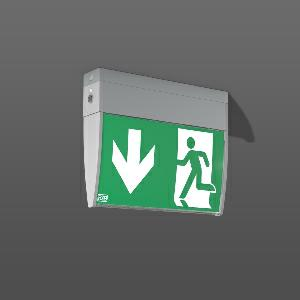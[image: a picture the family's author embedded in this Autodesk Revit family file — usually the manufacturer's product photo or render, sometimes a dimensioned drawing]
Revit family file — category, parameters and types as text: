
# Revit family: gsun_d_652219_004_79a5
name_source: partatom
category: Lighting Fixtures
units: mm (PartAtom-declared; Revit-internal decimal feet)

## family parameters
Cut with Voids When Loaded = No
Host = Face
Light Source = No
Part Type = Normal
Room Calculation Point = No
Round Connector Dimension = Use Diameter
Shared = No

## types (1)
- GSUN D
    Apparent Load = 0 VA
    Approval mark = CE
    Default Elevation = 1800 mm
    Description = Series: GSUN D
Luminaire for escape route identification. Housing: extruded aluminium profile, powder-coated. 4 legends and 1 white lay in plastic sheet included. Universal mounting kit for ceiling and wall surface mounting. Electronic ballast included. Self-contained system with automatic self-test. With NFC programming interface. 
Colour: silver
Length: 247 mm
Width: 45 mm
Height: 200 mm
Weight: 0.9 kg
Operating mode: maintained power mode
Viewing Distance: 24 m
Duration time: 1 h, 3 h, 8 h
Lamp: LED
Socket: without socket
Colour temperature: 4000K
System power: 2 W
Control gear: Regulated power supply
Protection class: I
Type of protection: IP 30
    Height = 200 mm
    Lamp = 0 x
    Length = 247 mm
    Luminous efficacy = 0 lm/W
    Manufacturer = RZB
    ModVariant = No
    Model = 652219.004
    Mounting Place = Ceiling, Wall
    Mounting Type = Surface mounted
    Number of Poles = 1
    OnlyDefault = Yes
    Power Factor = 1
    Product Name = GSUN D
    Product group = Surface mounted ceiling and wall luminaires
    ProductGroupID = 305
    Protection Class = Protection class I
    Protection Degree = IP 30
    RLX_Detail_Level = 1
    RLX_Emergency_Light_Flux = 0 lm
    RLX_Emergency_Type = 0
    RLX_Emergency_Type_DB = No
    RlxData = <blob elided: 30289 chars, md5=d1ba1124>
    Standby Power = 0 W
    System Light Flux = 0 lm
    System Power = 0 W
    Type Comments = Product without accessories
    Type Image = 671995.004.1.jpg
    URL = http://relux.com
    VarID = ---
    Voltage = 230 V
    Voltage Range = 220-240 V
    Weight = 0.00 kg
    Width = 45 mm

## geometry (parser evidence)
native form markers: Blend x4, Sweep x9
no freeform markers — native parametric forms only
